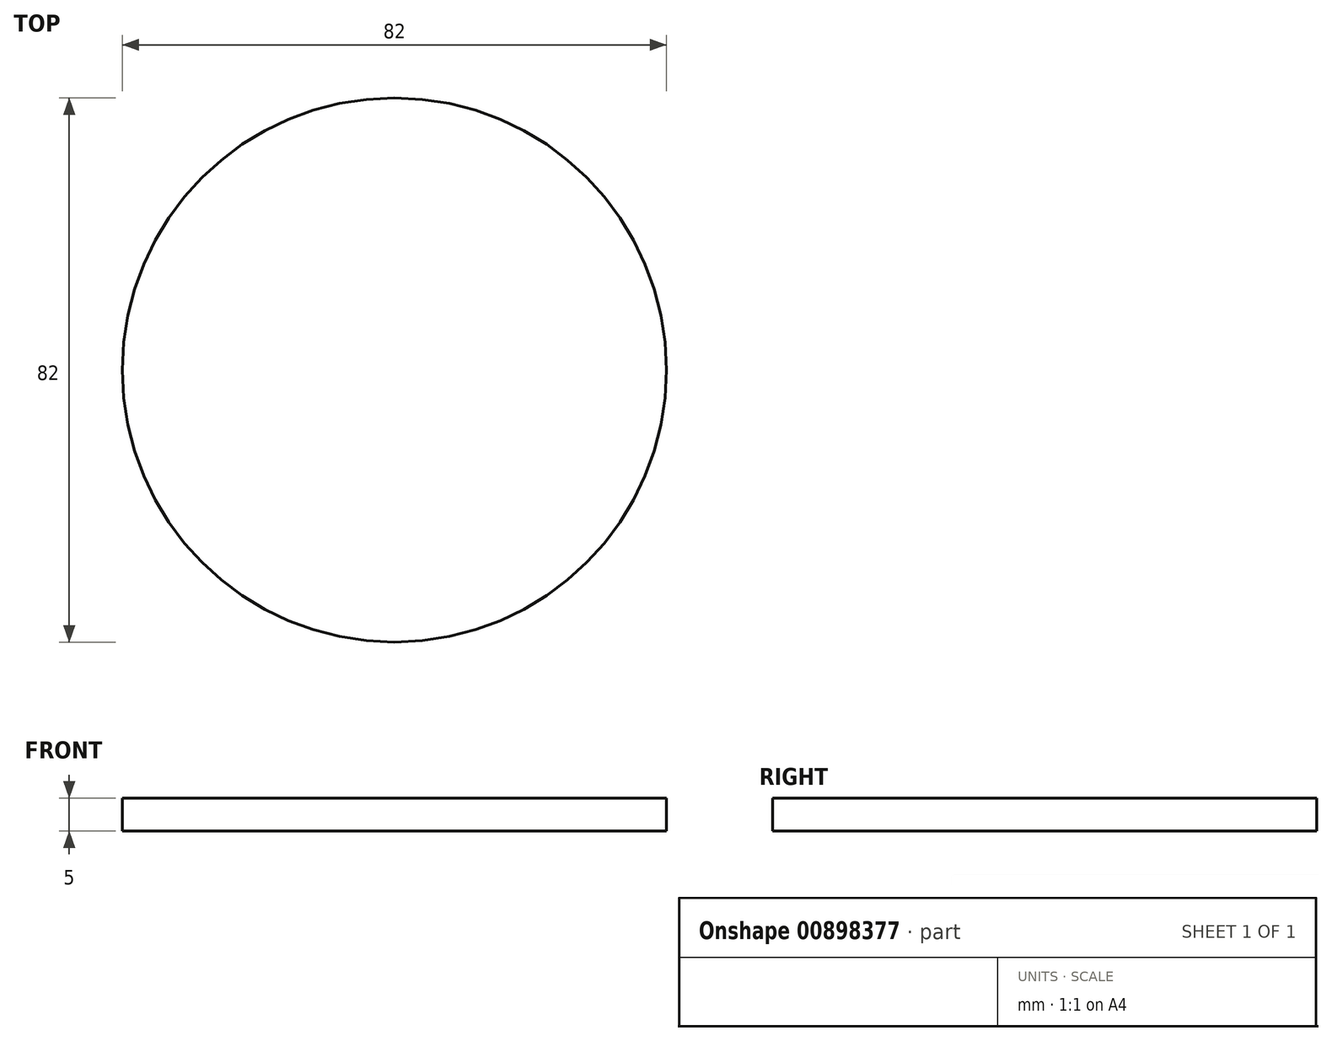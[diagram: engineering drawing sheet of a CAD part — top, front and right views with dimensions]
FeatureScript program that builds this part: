
annotation { "Feature Type Name" : "Feature", "Feature Type Description" : "" }
export const myFeature = defineFeature(function(context is Context, id is Id, definition is map)
    precondition{}
    {
        {
            var Q0;
            Q0=qCreatedBy(makeId("Top.planeOp"),FACE);
            var sketch = newSketch(context, id + "F0", { "sketchPlane" : qUnion([Q0])});
            skCircle(sketch, "E0", {"center": v(0, 0) * mm, "radius": 41 * mm});
            skSolve(sketch);
        }
        {
            var Q0;
            Q0=makeQuery(id+"F0.imprint","IMPRINT",FACE,{"disambiguationData":[TD([[makeQuery(id+"F0.imprint","IMPRINT",EDGE,{"derivedFrom":sQuery(id+"F0.wireOp",EDGE,"E0")}),1.0]])]});
            extrude(context, id + "F1", {"entities" : qUnion([Q0]), "depth" : 5 * mm, "offsetDistance" : 25 * mm});
        }
    });
